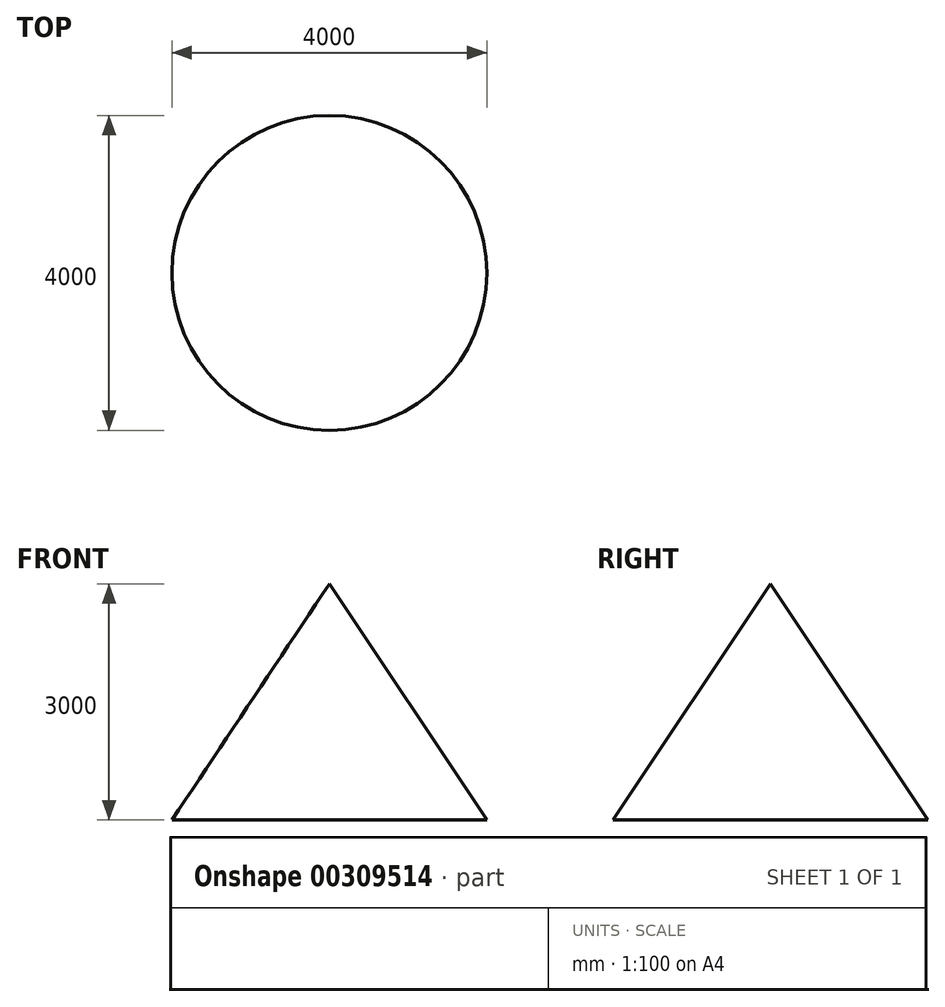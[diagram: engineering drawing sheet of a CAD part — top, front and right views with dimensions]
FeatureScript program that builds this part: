
annotation { "Feature Type Name" : "Feature", "Feature Type Description" : "" }
export const myFeature = defineFeature(function(context is Context, id is Id, definition is map)
    precondition{}
    {
        {
            var Q0;
            Q0=qCreatedBy(makeId("Front.planeOp"),FACE);
            var sketch = newSketch(context, id + "F0", { "sketchPlane" : qUnion([Q0])});
            skLineSegment(sketch, "E0", {"start": v(0, 0) * mm, "end": v(2000, -3000) * mm});
            skLineSegment(sketch, "E1", {"start": v(2000, -3000) * mm, "end": v(0, -3000) * mm});
            skLineSegment(sketch, "E2", {"start": v(0, -3000) * mm, "end": v(0, 0) * mm});
            skLineSegment(sketch, "E3", {"start": v(0, 7.99) * mm, "end": v(0, -3056.84) * mm, "construction": true});
            skSolve(sketch);
        }
        {
            var Q0;
            Q0=makeQuery(id+"F0.imprint","IMPRINT",FACE,{"disambiguationData":[TD([[makeQuery(id+"F0.imprint","IMPRINT",EDGE,{"derivedFrom":sQuery(id+"F0.wireOp",EDGE,"E0")}),-1.0]])]});
            var Q1;
            Q1=sQuery(id+"F0.wireOp",EDGE,"E3");
            revolve(context, id + "F1", {"entities" : qUnion([Q0]), "axis" : qUnion([Q1]), "revolveType" : RevolveType.FULL});
        }
    });
